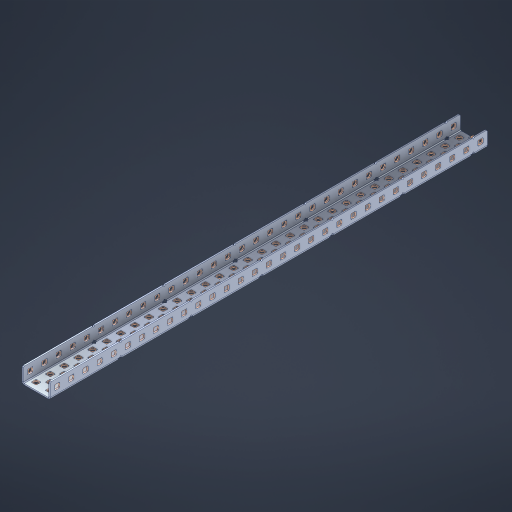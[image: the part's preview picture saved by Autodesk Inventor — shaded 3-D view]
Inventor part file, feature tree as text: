
AUTODESK INVENTOR PART (.ipt)
format: ipt  version: 2023 (Build 270158000, 158)  size: 1,928,192 bytes
history: native  units: in
note: dims shown in document units (in); Inventor stores cm internally (conversion verified against a paired STEP export)
features: other x162, extrude x153, sheet_metal_op x11, sketch x10, pattern_linear x2, mirror x1, chamfer x1
ambient origin geometry x8: Origin, YZ Plane, XZ Plane, XY Plane, X Axis, Y Axis, Z Axis, Center Point
bodies: Solid1 (feature_tree), Body (feature_tree)
feature tree (340):
  sheet_metal_op  "Flanges"
  other  "Flange Pattern Plane"
  other  "Flange Pattern Sketch"
  sheet_metal_op  "Flange Pattern"
  sheet_metal_op  "Body Pattern"
  pattern_linear  "Center Pattern"  Spacing1=0.0469in  [1 undecoded]
  other  "Arc Length"
  mirror  "Notch Mirror"
  pattern_linear  "Notch Pattern"  Spacing1=0.182in  [1 undecoded]
  chamfer  "End Chamfer"
  extrude  "Half Cut"  Depth=0.02in
  sketch  "Sketch1"  dims[d0=1.0in]
  other  "Plate1"
  sketch  "Sketch2"  dims[d1=15.5in]
  other  "Plate2"
  sheet_metal_op  "Bend1"
  sheet_metal_op  "Corner1"
  sketch  "Sketch3"  dims[d2=0.0469in]
  sketch  "Sketch7"  dims[d3=0.0469in]
  other  "Srf1"
  other  "Srf2"
  sketch  "Sketch8"  dims[d4=0.0234in]
  sketch  "Sketch9"  dims[d5=0.0938in]
  other  "Srf91"
  sheet_metal_op  "Body Pattern Sketch"
  other  "Srf92"
  sketch  "Sketch13"  dims[d6=0.0469in]
  sketch  "Sketch14"  dims[d7=0.5in d8=90.0deg d9=0.0312in]
  sketch  "Sketch15"  dims[d10=0.1875in]
  sketch  "Sketch16"  dims[d11=0.0469in d12=0.0469in d16=0.182in d17=0.02in d18=0.0469in d19=0.0in d20=0.25in d21=0.25in d38=12.2047in d40=0.5in d41=0.7874in d43=1.0in d46=0.172in d47=1.0in d48=0.0in d49=0.182in d50=0.02in d51=0.25in d52=0.25in d53=0.0469in d54=0.0in d55=0.172in d56=1.0in d57=0.0in d58=0.25in d60=12.2047in d62=0.5in d63=0.7874in d65=0.5in d85=0.1227in d86=0.1659in d88=0.04in d89=0.0469in d90=0.0in d91=0.04in d92=0.0491in d95=2.5in d96=0.04in d97=0.25in d98=45.0deg d99=0.25in d100=0.5in d101=0.0in d102=2.497in d106=0.182in d107=0.02in d108=0.5in d109=0.5in d110=0.0469in d111=0.0in d112=0.172in d113=0.5in d114=0.0in d117=0.5in d118=0.5in d119=0.5in]
  other  "Srf786"
  other  "Srf823"
  other  "Srf824"
  other  "Srf825"
  other  "Srf826"
  other  "Srf827"
  other  "Srf828"
  other  "Srf829"
  other  "Srf856"
  other  "Srf857"
  other  "Srf858"
  other  "Srf859"
  other  "Srf860"
  other  "Srf861"
  other  "Srf862"
  other  "Srf889"
  other  "Srf890"
  other  "Srf891"
  other  "Srf892"
  other  "Srf893"
  other  "Srf894"
  other  "Srf895"
  other  "Srf896"
  other  "Srf922"
  other  "Srf923"
  other  "Srf924"
  other  "Srf925"
  other  "Srf926"
  other  "Srf959"
  other  "Srf960"
  other  "Srf961"
  other  "Srf962"
  other  "Srf963"
  other  "Srf996"
  other  "Srf997"
  other  "Srf998"
  other  "Srf999"
  other  "Srf1000"
  other  "Srf1143"
  other  "Srf1144"
  other  "Srf1145"
  other  "Srf1146"
  other  "Srf1147"
  other  "Srf1148"
  other  "Srf1149"
  other  "Srf1150"
  other  "Srf1151"
  other  "Srf1152"
  other  "Srf1153"
  other  "Srf1154"
  other  "Srf1155"
  other  "Srf1156"
  other  "Srf1157"
  other  "Srf1158"
  other  "Srf1159"
  other  "Srf1160"
  other  "Srf1161"
  other  "Srf1162"
  other  "Srf1163"
  other  "Srf1164"
  other  "Srf1165"
  other  "Srf1166"
  other  "Srf1167"
  other  "Srf1168"
  other  "Srf1169"
  other  "Srf1170"
  other  "Srf1171"
  other  "Srf1172"
  other  "Srf1173"
  other  "Srf1174"
  other  "Srf1175"
  other  "Srf1176"
  other  "Srf1177"
  other  "Srf1178"
  other  "Srf1179"
  other  "Srf1180"
  other  "Srf1181"
  other  "Srf1182"
  other  "Srf1183"
  other  "Srf1184"
  other  "Srf1185"
  other  "Srf1186"
  other  "Srf1187"
  other  "Srf1188"
  other  "Srf1189"
  other  "Srf1190"
  other  "Srf1199"
  other  "Srf1200"
  other  "Srf1201"
  other  "Srf1202"
  other  "Srf1203"
  other  "Srf1204"
  other  "Srf1205"
  other  "Srf1206"
  other  "Srf1207"
  other  "Srf1208"
  other  "Srf1209"
  other  "Srf1210"
  other  "Srf1211"
  other  "Srf1212"
  other  "Srf1213"
  other  "Srf1214"
  other  "Srf1215"
  other  "Srf1216"
  other  "Srf1217"
  other  "Srf1218"
  other  "Srf1219"
  other  "Srf1220"
  other  "Srf1221"
  other  "Srf1222"
  other  "Srf1223"
  other  "Srf1224"
  other  "Srf1225"
  other  "Srf1226"
  other  "Srf1227"
  other  "Srf1228"
  other  "Srf1229"
  other  "Srf1230"
  other  "Srf1231"
  other  "Srf1232"
  other  "Srf1233"
  other  "Srf1234"
  other  "Srf1235"
  other  "Srf1236"
  other  "Srf1237"
  other  "Srf1238"
  other  "Srf1239"
  other  "Srf1240"
  other  "Srf1241"
  other  "Srf1242"
  other  "Srf1243"
  other  "Srf1244"
  other  "Srf1245"
  other  "Srf1246"
  other  "Srf1255"
  other  "Srf1256"
  other  "Srf1257"
  other  "Srf1258"
  other  "Srf1259"
  other  "Srf1260"
  other  "Srf1261"
  other  "Srf1262"
  other  "Srf1263"
  other  "Srf1264"
  other  "Srf1265"
  other  "Srf1266"
  other  "Srf1267"
  other  "Srf1268"
  other  "Srf1269"
  other  "Srf1270"
  other  "Srf1271"
  sheet_metal_op  "Flange Stamp"
  sheet_metal_op  "Flange Circle"
  sheet_metal_op  "Body Stamp"
  sheet_metal_op  "Body Circle"
  other  "Center Stamp"
  other  "Center Circle"
  sheet_metal_op  "Notch"
  extrude  "ExtrusionSrf2"  Depth=0.0469in
  extrude  "ExtrusionSrf92"  TaperAngle=0.0deg  [1 undecoded]
  extrude  "ExtrusionSrf823"  Depth=0.5in
  extrude  "ExtrusionSrf824"  Depth=0.5in
  extrude  "ExtrusionSrf825"  Depth=0.5in
  extrude  "ExtrusionSrf826"  Depth=0.5in
  extrude  "ExtrusionSrf827"  Depth=1.0in TaperAngle=0.0deg
  extrude  "ExtrusionSrf828"  Depth=0.5in
  extrude  "ExtrusionSrf829"  Depth=0.02in
  extrude  "ExtrusionSrf856"  Depth=0.5in
  extrude  "ExtrusionSrf857"  Depth=0.5in
  extrude  "ExtrusionSrf858"  Depth=0.0469in
  extrude  "ExtrusionSrf859"  TaperAngle=0.0deg  [1 undecoded]
  extrude  "ExtrusionSrf860"  Depth=0.5in
  extrude  "ExtrusionSrf861"  Depth=1.0in TaperAngle=0.0deg
  extrude  "ExtrusionSrf862"  Depth=0.5in
  extrude  "ExtrusionSrf889"  Depth=0.5in
  extrude  "ExtrusionSrf890"  Depth=0.5in
  extrude  "ExtrusionSrf891"  Depth=0.5in
  extrude  "ExtrusionSrf892"  Depth=0.5in
  extrude  "ExtrusionSrf893"  Depth=0.5in
  extrude  "ExtrusionSrf894"  Depth=0.0469in
  extrude  "ExtrusionSrf895"  TaperAngle=0.0deg  [1 undecoded]
  extrude  "ExtrusionSrf896"  Depth=0.5in
  extrude  "ExtrusionSrf922"  Depth=0.5in
  extrude  "ExtrusionSrf923"  Depth=2.5in
  extrude  "ExtrusionSrf924"  Depth=0.5in TaperAngle=45.0deg
  extrude  "ExtrusionSrf925"  Depth=0.5in
  extrude  "ExtrusionSrf926"  Depth=0.5in TaperAngle=0.0deg
  extrude  "ExtrusionSrf959"  Depth=0.5in
  extrude  "ExtrusionSrf960"  Depth=0.5in
  extrude  "ExtrusionSrf961"  Depth=0.02in
  extrude  "ExtrusionSrf962"  Depth=0.5in
  extrude  "ExtrusionSrf963"  Depth=0.5in
  extrude  "ExtrusionSrf996"  Depth=0.0469in
  extrude  "ExtrusionSrf997"  TaperAngle=0.0deg  [1 undecoded]
  extrude  "ExtrusionSrf998"  Depth=0.5in
  extrude  "ExtrusionSrf999"  Depth=0.5in TaperAngle=0.0deg
  extrude  "ExtrusionSrf1000"  Depth=0.5in
  extrude  "ExtrusionSrf1143"  Depth=0.5in
  extrude  "ExtrusionSrf1144"  Depth=0.5in
  extrude  "ExtrusionSrf1145"  [1 undecoded]
  extrude  "ExtrusionSrf1146"  [1 undecoded]
  extrude  "ExtrusionSrf1147"  [1 undecoded]
  extrude  "ExtrusionSrf1148"  [1 undecoded]
  extrude  "ExtrusionSrf1149"  [1 undecoded]
  extrude  "ExtrusionSrf1150"  [1 undecoded]
  extrude  "ExtrusionSrf1151"  [1 undecoded]
  extrude  "ExtrusionSrf1152"  [1 undecoded]
  extrude  "ExtrusionSrf1153"  [1 undecoded]
  extrude  "ExtrusionSrf1154"  [1 undecoded]
  extrude  "ExtrusionSrf1155"  [1 undecoded]
  extrude  "ExtrusionSrf1156"  [1 undecoded]
  extrude  "ExtrusionSrf1157"  [1 undecoded]
  extrude  "ExtrusionSrf1158"  [1 undecoded]
  extrude  "ExtrusionSrf1159"  [1 undecoded]
  extrude  "ExtrusionSrf1160"  [1 undecoded]
  extrude  "ExtrusionSrf1161"  [1 undecoded]
  extrude  "ExtrusionSrf1162"  [1 undecoded]
  extrude  "ExtrusionSrf1163"  [1 undecoded]
  extrude  "ExtrusionSrf1164"  [1 undecoded]
  extrude  "ExtrusionSrf1165"  [1 undecoded]
  extrude  "ExtrusionSrf1166"  [1 undecoded]
  extrude  "ExtrusionSrf1167"  [1 undecoded]
  extrude  "ExtrusionSrf1168"  [1 undecoded]
  extrude  "ExtrusionSrf1169"  [1 undecoded]
  extrude  "ExtrusionSrf1170"  [1 undecoded]
  extrude  "ExtrusionSrf1171"  [1 undecoded]
  extrude  "ExtrusionSrf1172"  [1 undecoded]
  extrude  "ExtrusionSrf1173"  [1 undecoded]
  extrude  "ExtrusionSrf1174"  [1 undecoded]
  extrude  "ExtrusionSrf1175"  [1 undecoded]
  extrude  "ExtrusionSrf1176"  [1 undecoded]
  extrude  "ExtrusionSrf1177"  [1 undecoded]
  extrude  "ExtrusionSrf1178"  [1 undecoded]
  extrude  "ExtrusionSrf1179"  [1 undecoded]
  extrude  "ExtrusionSrf1180"  [1 undecoded]
  extrude  "ExtrusionSrf1181"  [1 undecoded]
  extrude  "ExtrusionSrf1182"  [1 undecoded]
  extrude  "ExtrusionSrf1183"  [1 undecoded]
  extrude  "ExtrusionSrf1184"  [1 undecoded]
  extrude  "ExtrusionSrf1185"  [1 undecoded]
  extrude  "ExtrusionSrf1186"  [1 undecoded]
  extrude  "ExtrusionSrf1187"  [1 undecoded]
  extrude  "ExtrusionSrf1188"  [1 undecoded]
  extrude  "ExtrusionSrf1189"  [1 undecoded]
  extrude  "ExtrusionSrf1190"  [1 undecoded]
  extrude  "ExtrusionSrf1199"  [1 undecoded]
  extrude  "ExtrusionSrf1200"  [1 undecoded]
  extrude  "ExtrusionSrf1201"  [1 undecoded]
  extrude  "ExtrusionSrf1202"  [1 undecoded]
  extrude  "ExtrusionSrf1203"  [1 undecoded]
  extrude  "ExtrusionSrf1204"  [1 undecoded]
  extrude  "ExtrusionSrf1205"  [1 undecoded]
  extrude  "ExtrusionSrf1206"  [1 undecoded]
  extrude  "ExtrusionSrf1207"  [1 undecoded]
  extrude  "ExtrusionSrf1208"  [1 undecoded]
  extrude  "ExtrusionSrf1209"  [1 undecoded]
  extrude  "ExtrusionSrf1210"  [1 undecoded]
  extrude  "ExtrusionSrf1211"  [1 undecoded]
  extrude  "ExtrusionSrf1212"  [1 undecoded]
  extrude  "ExtrusionSrf1213"  [1 undecoded]
  extrude  "ExtrusionSrf1214"  [1 undecoded]
  extrude  "ExtrusionSrf1215"  [1 undecoded]
  extrude  "ExtrusionSrf1216"  [1 undecoded]
  extrude  "ExtrusionSrf1217"  [1 undecoded]
  extrude  "ExtrusionSrf1218"  [1 undecoded]
  extrude  "ExtrusionSrf1219"  [1 undecoded]
  extrude  "ExtrusionSrf1220"  [1 undecoded]
  extrude  "ExtrusionSrf1221"  [1 undecoded]
  extrude  "ExtrusionSrf1222"  [1 undecoded]
  extrude  "ExtrusionSrf1223"  [1 undecoded]
  extrude  "ExtrusionSrf1224"  [1 undecoded]
  extrude  "ExtrusionSrf1225"  [1 undecoded]
  extrude  "ExtrusionSrf1226"  [1 undecoded]
  extrude  "ExtrusionSrf1227"  [1 undecoded]
  extrude  "ExtrusionSrf1228"  [1 undecoded]
  extrude  "ExtrusionSrf1229"  [1 undecoded]
  extrude  "ExtrusionSrf1230"  [1 undecoded]
  extrude  "ExtrusionSrf1231"  [1 undecoded]
  extrude  "ExtrusionSrf1232"  [1 undecoded]
  extrude  "ExtrusionSrf1233"  [1 undecoded]
  extrude  "ExtrusionSrf1234"  [1 undecoded]
  extrude  "ExtrusionSrf1235"  [1 undecoded]
  extrude  "ExtrusionSrf1236"  [1 undecoded]
  extrude  "ExtrusionSrf1237"  [1 undecoded]
  extrude  "ExtrusionSrf1238"  [1 undecoded]
  extrude  "ExtrusionSrf1239"  [1 undecoded]
  extrude  "ExtrusionSrf1240"  [1 undecoded]
  extrude  "ExtrusionSrf1241"  [1 undecoded]
  extrude  "ExtrusionSrf1242"  [1 undecoded]
  extrude  "ExtrusionSrf1243"  [1 undecoded]
  extrude  "ExtrusionSrf1244"  [1 undecoded]
  extrude  "ExtrusionSrf1245"  [1 undecoded]
  extrude  "ExtrusionSrf1246"  [1 undecoded]
  extrude  "ExtrusionSrf1255"  [1 undecoded]
  extrude  "ExtrusionSrf1256"  [1 undecoded]
  extrude  "ExtrusionSrf1257"  [1 undecoded]
  extrude  "ExtrusionSrf1258"  [1 undecoded]
  extrude  "ExtrusionSrf1259"  [1 undecoded]
  extrude  "ExtrusionSrf1260"  [1 undecoded]
  extrude  "ExtrusionSrf1261"  [1 undecoded]
  extrude  "ExtrusionSrf1262"  [1 undecoded]
  extrude  "ExtrusionSrf1263"  [1 undecoded]
  extrude  "ExtrusionSrf1264"  [1 undecoded]
  extrude  "ExtrusionSrf1265"  [1 undecoded]
  extrude  "ExtrusionSrf1266"  [1 undecoded]
  extrude  "ExtrusionSrf1267"  [1 undecoded]
  extrude  "ExtrusionSrf1268"  [1 undecoded]
  extrude  "ExtrusionSrf1269"  [1 undecoded]
  extrude  "ExtrusionSrf1270"  [1 undecoded]
  extrude  "ExtrusionSrf1271"  [1 undecoded]
note: 117 required parameter values undecoded (feature->parameter linkage not recoverable at this tier; creation-order binding heuristic only, values carry confidence <= 0.55)
